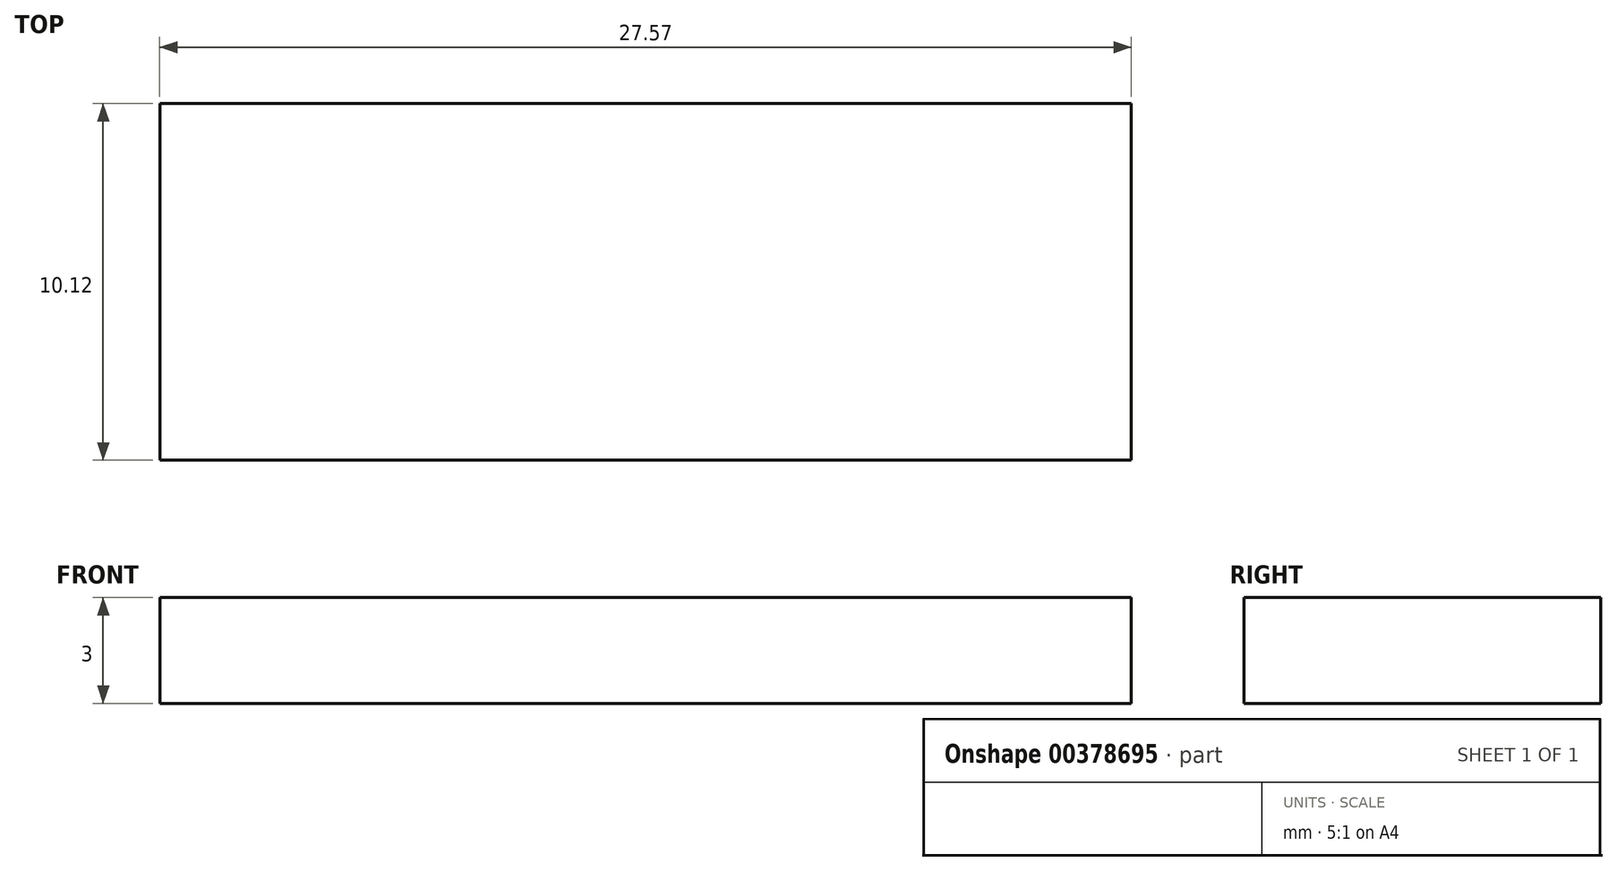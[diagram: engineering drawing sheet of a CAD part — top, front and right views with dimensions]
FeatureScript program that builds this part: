
annotation { "Feature Type Name" : "Feature", "Feature Type Description" : "" }
export const myFeature = defineFeature(function(context is Context, id is Id, definition is map)
    precondition{}
    {
        {
            var Q0;
            Q0=qCreatedBy(makeId("Top.planeOp"),FACE);
            var sketch = newSketch(context, id + "F0", { "sketchPlane" : qUnion([Q0])});
            skLineSegment(sketch, "E0.bottom", {"start": v(-11.89, 4.08) * mm, "end": v(15.68, 4.08) * mm});
            skLineSegment(sketch, "E0.top", {"start": v(-11.89, -6.04) * mm, "end": v(15.68, -6.04) * mm});
            skLineSegment(sketch, "E0.left", {"start": v(-11.89, 4.08) * mm, "end": v(-11.89, -6.04) * mm});
            skLineSegment(sketch, "E0.right", {"start": v(15.68, 4.08) * mm, "end": v(15.68, -6.04) * mm});
            skSolve(sketch);
        }
        {
            var Q0;
            Q0=qSketchRegion(id+"F0",true);
            extrude(context, id + "F1", {"entities" : qUnion([Q0]), "depth" : 3 * mm});
        }
    });
